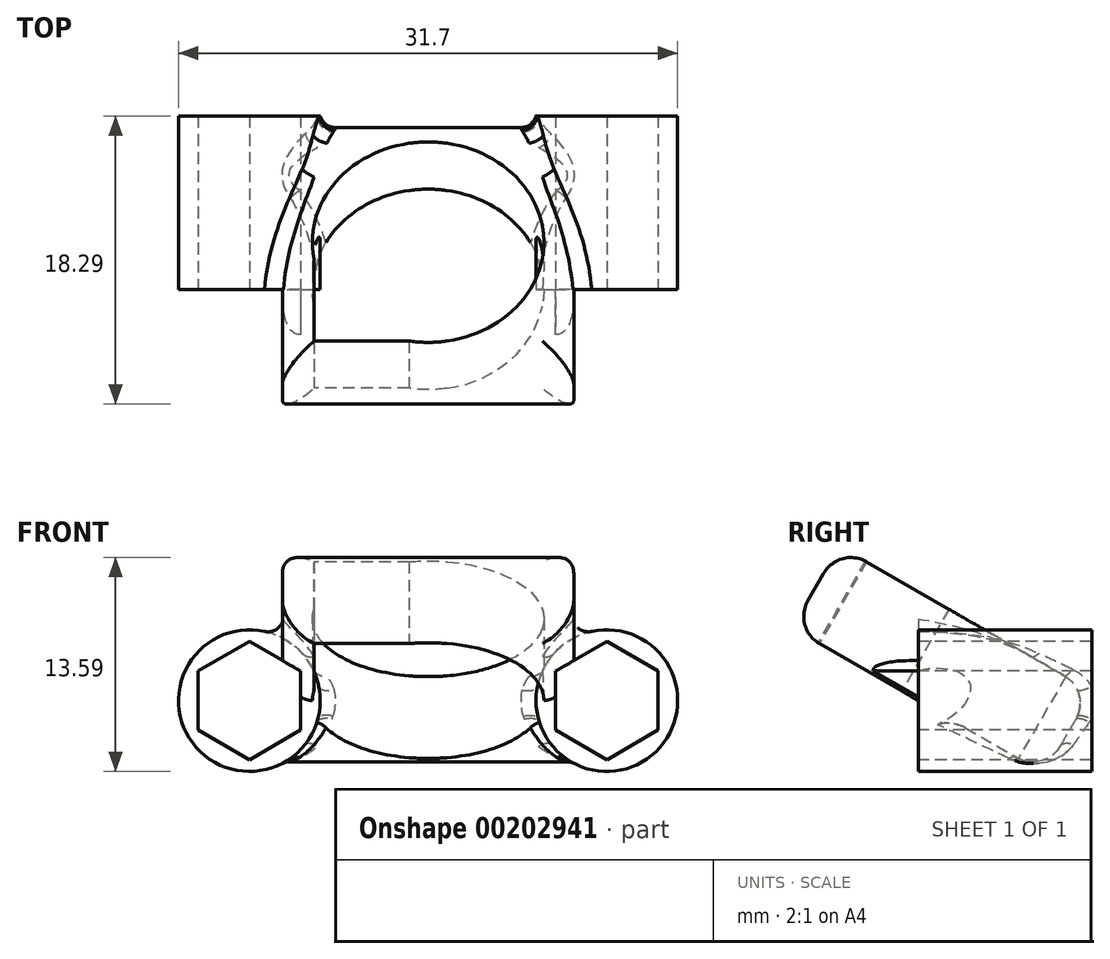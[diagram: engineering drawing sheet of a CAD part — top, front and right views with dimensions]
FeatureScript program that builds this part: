
annotation { "Feature Type Name" : "Feature", "Feature Type Description" : "" }
export const myFeature = defineFeature(function(context is Context, id is Id, definition is map)
    precondition{}
    {
        {
            var Q0;
            Q0=qCreatedBy(makeId("Top.planeOp"),FACE);
            var sketch = newSketch(context, id + "F0", { "sketchPlane" : qUnion([Q0])});
            skCircle(sketch, "E0", {"center": v(0, 0) * mm, "radius": 7.35 * mm});
            skLineSegment(sketch, "E1.bottom", {"start": v(9.25, 9.25) * mm, "end": v(-9.25, 9.25) * mm});
            skLineSegment(sketch, "E1.top", {"start": v(9.25, -9.25) * mm, "end": v(-9.25, -9.25) * mm});
            skLineSegment(sketch, "E1.left", {"start": v(9.25, 9.25) * mm, "end": v(9.25, -9.25) * mm});
            skLineSegment(sketch, "E1.right", {"start": v(-9.25, 9.25) * mm, "end": v(-9.25, -9.25) * mm});
            skSolve(sketch);
        }
        {
            var Q0;
            Q0=makeQuery(id+"F0.imprint","IMPRINT",FACE,{"disambiguationData":[TD([[makeQuery(id+"F0.imprint","IMPRINT",EDGE,{"derivedFrom":sQuery(id+"F0.wireOp",EDGE,"E0")}),-1.0]])]});
            extrude(context, id + "F1", {"entities" : qUnion([Q0]), "depth" : 6 * mm});
        }
        {
            var Q0;
            Q0=qCreatedBy(makeId("Top.planeOp"),FACE);
            var sketch = newSketch(context, id + "F2", { "sketchPlane" : qUnion([Q0])});
            skLineSegment(sketch, "E2", {"start": v(-15.14, 0) * mm, "end": v(14.33, 0) * mm});
            skSolve(sketch);
        }
        {
            var Q0;
            Q0=makeQuery(id+"F1.opExtrude","SWEPT_BODY",BODY,{"disambiguationData":[OSD([sQuery(id+"F0.wireOp",EDGE,"E0"),sQuery(id+"F0.wireOp",EDGE,"E1.bottom"),sQuery(id+"F0.wireOp",EDGE,"E1.top"),sQuery(id+"F0.wireOp",EDGE,"E1.left"),sQuery(id+"F0.wireOp",EDGE,"E1.right")])]});
            var Q1;
            Q1=sQuery(id+"F2.wireOp",EDGE,"E2");
            var Q2;
            Q2=sQuery(id+"F2.wireOp",EDGE,"E2");
            transform(context, id + "F3", {"entities" : qUnion([Q0]), "transformType" : TransformType.ROTATION, "transformAxis" : qUnion([Q2]), "angle" : 30 * degree, "oppositeDirection" : true, "makeCopy" : false});
        }
        {
            var Q0;
            Q0=qCreatedBy(makeId("Front.planeOp"),FACE);
            var sketch = newSketch(context, id + "F4", { "sketchPlane" : qUnion([Q0])});
            skCircle(sketch, "E3.cCircle", {"center": v(-11.35, 0) * mm, "radius": 3.25 * mm, "construction": true});
            skLineSegment(sketch, "E3.0", {"start": v(-8.1, 1.88) * mm, "end": v(-8.1, -1.88) * mm});
            skLineSegment(sketch, "E3.1", {"start": v(-8.1, -1.88) * mm, "end": v(-11.35, -3.75) * mm});
            skLineSegment(sketch, "E3.2", {"start": v(-11.35, -3.75) * mm, "end": v(-14.6, -1.88) * mm});
            skLineSegment(sketch, "E3.3", {"start": v(-14.6, -1.88) * mm, "end": v(-14.6, 1.88) * mm});
            skLineSegment(sketch, "E3.4", {"start": v(-14.6, 1.88) * mm, "end": v(-11.35, 3.75) * mm});
            skLineSegment(sketch, "E3.5", {"start": v(-11.35, 3.75) * mm, "end": v(-8.1, 1.88) * mm});
            skPoint(sketch, "E3.0.midPoint", {"position": v(-8.1, 0) * mm});
            skCircle(sketch, "E4", {"center": v(-11.35, 0) * mm, "radius": 4.5 * mm});
            skCircle(sketch, "E5.1.0.0", {"center": v(11.35, 0) * mm, "radius": 4.5 * mm});
            skLineSegment(sketch, "E5.1.0.1", {"start": v(11.35, 3.75) * mm, "end": v(14.6, 1.88) * mm});
            skLineSegment(sketch, "E5.1.0.2", {"start": v(8.1, 1.88) * mm, "end": v(11.35, 3.75) * mm});
            skLineSegment(sketch, "E5.1.0.3", {"start": v(8.1, -1.88) * mm, "end": v(8.1, 1.88) * mm});
            skLineSegment(sketch, "E5.1.0.4", {"start": v(11.35, -3.75) * mm, "end": v(8.1, -1.88) * mm});
            skLineSegment(sketch, "E5.1.0.5", {"start": v(14.6, -1.88) * mm, "end": v(11.35, -3.75) * mm});
            skLineSegment(sketch, "E5.1.0.6", {"start": v(14.6, 1.88) * mm, "end": v(14.6, -1.88) * mm});
            skCircle(sketch, "E5.1.0.7", {"center": v(11.35, 0) * mm, "radius": 3.25 * mm, "construction": true});
            skPoint(sketch, "E5.1.0.8", {"position": v(14.6, 0) * mm});
            skCircle(sketch, "E5.2.0.0", {"center": v(34.05, 0) * mm, "radius": 4.5 * mm});
            skLineSegment(sketch, "E5.2.0.1", {"start": v(34.05, 3.75) * mm, "end": v(37.3, 1.88) * mm});
            skLineSegment(sketch, "E5.2.0.2", {"start": v(30.8, 1.88) * mm, "end": v(34.05, 3.75) * mm});
            skLineSegment(sketch, "E5.2.0.3", {"start": v(30.8, -1.88) * mm, "end": v(30.8, 1.88) * mm});
            skLineSegment(sketch, "E5.2.0.4", {"start": v(34.05, -3.75) * mm, "end": v(30.8, -1.88) * mm});
            skLineSegment(sketch, "E5.2.0.5", {"start": v(37.3, -1.88) * mm, "end": v(34.05, -3.75) * mm});
            skLineSegment(sketch, "E5.2.0.6", {"start": v(37.3, 1.88) * mm, "end": v(37.3, -1.88) * mm});
            skCircle(sketch, "E5.2.0.7", {"center": v(34.05, 0) * mm, "radius": 3.25 * mm, "construction": true});
            skPoint(sketch, "E5.2.0.8", {"position": v(37.3, 0) * mm});
            skLineSegment(sketch, "E5.direction1", {"start": v(-14.6, -1.88) * mm, "end": v(8.1, -1.88) * mm, "construction": true});
            skSolve(sketch);
        }
        {
            var Q0;
            Q0=makeQuery(id+"F4.imprint","IMPRINT",FACE,{"disambiguationData":[TD([[makeQuery(id+"F4.imprint","IMPRINT",EDGE,{"derivedFrom":sQuery(id+"F4.wireOp",EDGE,"E5.1.0.0")}),1.0]])]});
            var Q1;
            Q1=makeQuery(id+"F4.imprint","IMPRINT",FACE,{"disambiguationData":[TD([[makeQuery(id+"F4.imprint","IMPRINT",EDGE,{"derivedFrom":sQuery(id+"F4.wireOp",EDGE,"E3.0")}),1.0]])]});
            var Q2;
            Q2=makeQuery(id+"F1.opExtrude","CAP_VERTEX",VERTEX,{"disambiguationData":[OSD([sQuery(id+"F0.wireOp",EDGE,"E1.bottom"),sQuery(id+"F0.wireOp",EDGE,"E1.right")])],"isStart":false});
            extrude(context, id + "F5", {"entities" : qUnion([Q0, Q1]), "operationType" : NewBodyOperationType.ADD, "endBound" : BoundingType.UP_TO_VERTEX, "oppositeDirection" : true, "endBoundEntityVertex" : qUnion([Q2]), "depth" : 11 * mm});
        }
        {
            var Q0;
            Q0=makeQuery(id+"F4.imprint","IMPRINT",FACE,{"disambiguationData":[TD([[makeQuery(id+"F4.imprint","IMPRINT",EDGE,{"derivedFrom":sQuery(id+"F4.wireOp",EDGE,"E3.0")}),-1.0]])]});
            var Q1;
            Q1=makeQuery(id+"F4.imprint","IMPRINT",FACE,{"disambiguationData":[TD([[makeQuery(id+"F4.imprint","IMPRINT",EDGE,{"derivedFrom":sQuery(id+"F4.wireOp",EDGE,"E5.1.0.1")}),-1.0]])]});
            extrude(context, id + "F6", {"entities" : qUnion([Q0, Q1]), "operationType" : NewBodyOperationType.REMOVE, "depth" : 50 * mm, "symmetric" : true});
        }
        {
            var Q0;
            {var subQ0=sQuery(id+"F4.wireOp",EDGE,"E4");var subQ1=sQuery(id+"F0.wireOp",EDGE,"E1.bottom");Q0=makeQuery(id+"F5.boolean.opBoolean","SPLIT",EDGE,{"disambiguationData":[TD([makeQuery(id+"F5.opExtrude","SWEPT_FACE",FACE,{"disambiguationData":[OSD([subQ0])]})])],"derivedFrom":makeQuery(id+"F1.opExtrude","CAP_EDGE",EDGE,{"disambiguationData":[OSD([subQ1])],"isStart":false})});}
            var Q1;
            {var subQ0=sQuery(id+"F0.wireOp",EDGE,"E1.right");var subQ1=sQuery(id+"F0.wireOp",EDGE,"E1.top");Q1=makeQuery(id+"F5.boolean.opBoolean","SPLIT",EDGE,{"disambiguationData":[TD([makeQuery(id+"F1.opExtrude","SWEPT_FACE",FACE,{"disambiguationData":[OSD([subQ1])]})])],"derivedFrom":makeQuery(id+"F1.opExtrude","CAP_EDGE",EDGE,{"disambiguationData":[OSD([subQ0])],"isStart":false})});}
            var Q2;
            Q2=makeQuery(id+"F1.opExtrude","CAP_EDGE",EDGE,{"disambiguationData":[OSD([sQuery(id+"F0.wireOp",EDGE,"E1.top")])],"isStart":false});
            var Q3;
            {var subQ0=sQuery(id+"F0.wireOp",EDGE,"E1.left");var subQ1=sQuery(id+"F0.wireOp",EDGE,"E1.top");Q3=makeQuery(id+"F5.boolean.opBoolean","SPLIT",EDGE,{"disambiguationData":[TD([makeQuery(id+"F1.opExtrude","SWEPT_FACE",FACE,{"disambiguationData":[OSD([subQ1])]})])],"derivedFrom":makeQuery(id+"F1.opExtrude","CAP_EDGE",EDGE,{"disambiguationData":[OSD([subQ0])],"isStart":false})});}
            var Q4;
            {var subQ0=sQuery(id+"F0.wireOp",EDGE,"E1.right");var subQ1=sQuery(id+"F0.wireOp",EDGE,"E1.top");Q4=makeQuery(id+"F5.boolean.opBoolean","SPLIT",EDGE,{"disambiguationData":[TD([makeQuery(id+"F1.opExtrude","SWEPT_FACE",FACE,{"disambiguationData":[OSD([subQ1])]})])],"derivedFrom":makeQuery(id+"F1.opExtrude","CAP_EDGE",EDGE,{"disambiguationData":[OSD([subQ0])],"isStart":true})});}
            var Q5;
            Q5=makeQuery(id+"F1.opExtrude","CAP_EDGE",EDGE,{"disambiguationData":[OSD([sQuery(id+"F0.wireOp",EDGE,"E1.top")])],"isStart":true});
            var Q6;
            {var subQ0=sQuery(id+"F0.wireOp",EDGE,"E1.left");var subQ1=sQuery(id+"F0.wireOp",EDGE,"E1.top");Q6=makeQuery(id+"F5.boolean.opBoolean","SPLIT",EDGE,{"disambiguationData":[TD([makeQuery(id+"F1.opExtrude","SWEPT_FACE",FACE,{"disambiguationData":[OSD([subQ1])]})])],"derivedFrom":makeQuery(id+"F1.opExtrude","CAP_EDGE",EDGE,{"disambiguationData":[OSD([subQ0])],"isStart":true})});}
            var Q7;
            Q7=makeQuery(id+"F1.opExtrude","CAP_EDGE",EDGE,{"disambiguationData":[OSD([sQuery(id+"F0.wireOp",EDGE,"E1.bottom")])],"isStart":true});
            fillet(context, id + "F7", {"entities" : qUnion([Q0, Q1, Q2, Q3, Q4, Q5, Q6, Q7]), "radius" : 2 * mm, "tangentPropagation" : true, "allowEdgeOverflow" : false});
        }
        {
            var Q0;
            {var subQ0=makeQuery(id+"F5.opExtrude","SWEPT_FACE",FACE,{"disambiguationData":[OSD([sQuery(id+"F4.wireOp",EDGE,"E4")])]});var subQ1=sQuery(id+"F0.wireOp",EDGE,"E1.right");var subQ2=sQuery(id+"F0.wireOp",EDGE,"E1.top");Q0=makeQuery(id+"F7.opFillet","BLEND_EDGE",EDGE,{"blendedFrom":[makeQuery(id+"F5.boolean.opBoolean","SPLIT",EDGE,{"disambiguationData":[TD([makeQuery(id+"F1.opExtrude","SWEPT_FACE",FACE,{"disambiguationData":[OSD([subQ2])]})])],"derivedFrom":makeQuery(id+"F1.opExtrude","CAP_EDGE",EDGE,{"disambiguationData":[OSD([subQ1])],"isStart":false})}),subQ0],"blendedInto":[subQ0]});}
            var Q1;
            {var subQ0=makeQuery(id+"F5.opExtrude","SWEPT_FACE",FACE,{"disambiguationData":[OSD([sQuery(id+"F4.wireOp",EDGE,"E5.1.0.0")])]});var subQ1=sQuery(id+"F0.wireOp",EDGE,"E1.left");var subQ2=sQuery(id+"F0.wireOp",EDGE,"E1.top");Q1=makeQuery(id+"F7.opFillet","BLEND_EDGE",EDGE,{"blendedFrom":[makeQuery(id+"F5.boolean.opBoolean","SPLIT",EDGE,{"disambiguationData":[TD([makeQuery(id+"F1.opExtrude","SWEPT_FACE",FACE,{"disambiguationData":[OSD([subQ2])]})])],"derivedFrom":makeQuery(id+"F1.opExtrude","CAP_EDGE",EDGE,{"disambiguationData":[OSD([subQ1])],"isStart":false})}),subQ0],"blendedInto":[subQ0]});}
            fillet(context, id + "F8", {"entities" : qUnion([Q0, Q1]), "radius" : 1 * mm, "tangentPropagation" : true, "allowEdgeOverflow" : false});
        }
        {
            var Q0;
            {var subQ0=sQuery(id+"F0.wireOp",EDGE,"E1.right");var subQ2=sQuery(id+"F0.wireOp",EDGE,"E1.top");var subQ3=sQuery(id+"F0.wireOp",EDGE,"E1.left");var subQ6=sQuery(id+"F0.wireOp",EDGE,"E0");Q0=makeQuery(id+"F7.opFillet","SPLIT",FACE,{"disambiguationData":[OD(1.0)],"derivedFrom":makeQuery(id+"F5.boolean.opBoolean","SPLIT",FACE,{"disambiguationData":[TD([makeQuery(id+"F1.opExtrude","SWEPT_FACE",FACE,{"disambiguationData":[OSD([subQ2])]})])],"derivedFrom":makeQuery(id+"F1.opExtrude","CAP_FACE",FACE,{"disambiguationData":[OSD([subQ6,sQuery(id+"F0.wireOp",EDGE,"E1.bottom"),subQ2,subQ3,subQ0])],"isStart":true})})});}
            var sketch = newSketch(context, id + "F9", { "sketchPlane" : qUnion([Q0])});
            skCircle(sketch, "E6", {"center": v(0, 0) * mm, "radius": 7.35 * mm});
            skSolve(sketch);
        }
        {
            var Q0;
            {var subQ0=sQuery(id+"F9.wireOp",EDGE,"E6");Q0=makeQuery(id+"F9.imprint","IMPRINT",FACE,{"disambiguationData":[TD([[makeQuery(id+"F9.imprint","IMPRINT",EDGE,{"disambiguationData":[OD(0.0)],"derivedFrom":subQ0}),1.0]])]});}
            extrude(context, id + "F10", {"entities" : qUnion([Q0]), "operationType" : NewBodyOperationType.REMOVE, "oppositeDirection" : true, "depth" : 50 * mm, "symmetric" : true});
        }
    });
